# Revit family: MC10LED
name_source: partatom
category: Lighting Fixtures
units: mm (PartAtom-declared; Revit-internal decimal feet)

## family parameters
Cut with Voids When Loaded = No
Host = Face
Light Source = Yes
OmniClass Number = 23.80.70.11.14.11
OmniClass Title = Downlights
Part Type = Normal
Room Calculation Point = No
Round Connector Dimension = Use Diameter
Shared = No

## types (2) — shared parameters
Apparent Load = 40 VA
Color Filter = 16777215
Default Elevation = 48.000"
Description = 10 Inch High Lumen LED Cylinder
Dimming Lamp Color Temperature Shift = <None>
Emit Shape Visible in Rendering = No
Emit from Circle Diameter = 8.000"
Glass = White Glass
Is 120V = Yes
Is 277V = No
Lamp = LED Lamp
Load Classification = Lighting
Manufacturer = Prescolite
Model = MC10LED
Photometric Web File = generic
Tilt Angle = -90.00°
URL = https://www.currentlighting.com
Voltage = 120 V
Wattage Comments = 40W

## per-type parameters (varying)
| type | Backbox | Housing |
| MC10LED - 26 Inch Housing | Matt Black | 23.500" |
| MC10LED - 30 Inch Housing | Matt White | 26.750" |

## geometry (parser evidence)
native form markers: Sweep x3
no freeform markers — native parametric forms only
